# Revit family: Basin-Pedestal-American_Standard-Estate-0900_Series
name_source: partatom
category: Plumbing Fixtures
revit_build: Autodesk Revit 2014 (Build: 20130308_1515(x64)
units: mm (PartAtom-declared; Revit-internal decimal feet)

## types (24) — shared parameters
ADA Compliant = Yes
Assembly Code = D2010310
Basin Shape = Rectangle
CW Connection = Yes
CWFU = 1.5
Cold Water Connection Diameter = 3/8"
Cold Water Connection Height = 24"
Cold Water Connection Radius = 3/16"
Cold Water Connection Width = 4"
Default Elevation = 36 5/8"
Description = Estate Pedestal Bathroom Sink
HW Connection = Yes
HWFU = 1.5
Height = 7 1/2"
Hot Water Connection Diameter = 3/8"
Hot Water Connection Height = 24"
Hot Water Connection Radius = 3/16"
Hot Water Connection Width = 4"
Length = 20"
Manufacturer = American Standard
Price = Prices may vary. Please consult Manufacturer Representative for most up-to-date price list.
Product Documentation Link = https://www.americanstandard-us.com
Product Page URL = https://www.americanstandard-us.com
URL = http://www.americanstandard-us.com
Vent Connection = No
WFU = 2
Waste Connection = Yes
Waste Connection Diameter = 1 1/4"
Waste Connection Height = 22"
Waste Connection Radius = 5/8"
Width = 24"

## per-type parameters (varying)
| type | 0029.000 Pedestal | Centerset Height | Finish | Hole Punch Location | Installation Type | Material |
| 0900.004.020 | No | 3" | Fire Clay-American Standard-020-White | 4" | Countertop | Fire Clay-American Standard-020-White |
| 0900.008.020 | No | 3" | Fire Clay-American Standard-020-White | 8" | Countertop | Fire Clay-American Standard-020-White |
| 0900.001.020 | No | 9" | Fire Clay-American Standard-020-White | 4" | Countertop | Fire Clay-American Standard-020-White |
| 0900.001.021 | No | 9" | Fire Clay-American Standard-021-Bone | 4" | Countertop | Fire Clay-American Standard-021-Bone |
| 0900.001.178 | No | 9" | Fire Clay-American Standard-178-Black | 4" | Countertop | Fire Clay-American Standard-178-Black |
| 0900.001.222 | No | 9" | Fire Clay-American Standard-222-Linen | 4" | Countertop | Fire Clay-American Standard-222-Linen |
| 0900.004.021 | No | 3" | Fire Clay-American Standard-021-Bone | 4" | Countertop | Fire Clay-American Standard-021-Bone |
| 0900.004.178 | No | 3" | Fire Clay-American Standard-178-Black | 4" | Countertop | Fire Clay-American Standard-178-Black |
| 0900.004.222 | No | 3" | Fire Clay-American Standard-222-Linen | 4" | Countertop | Fire Clay-American Standard-222-Linen |
| 0900.008.021 | No | 3" | Fire Clay-American Standard-021-Bone | 8" | Countertop | Fire Clay-American Standard-021-Bone |
| 0900.008.178 | No | 3" | Fire Clay-American Standard-178-Black | 8" | Countertop | Fire Clay-American Standard-178-Black |
| 0900.008.222 | No | 3" | Fire Clay-American Standard-222-Linen | 8" | Countertop | Fire Clay-American Standard-222-Linen |
| 0900.100.020 | Yes | 9" | Fire Clay-American Standard-020-White | 4" | Pedestal | Fire Clay-American Standard-020-White |
| 0900.100.021 | Yes | 9" | Fire Clay-American Standard-021-Bone | 4" | Pedestal | Fire Clay-American Standard-021-Bone |
| 0900.100.178 | Yes | 9" | Fire Clay-American Standard-178-Black | 4" | Pedestal | Fire Clay-American Standard-178-Black |
| 0900.100.222 | Yes | 9" | Fire Clay-American Standard-222-Linen | 4" | Pedestal | Fire Clay-American Standard-222-Linen |
| 0900.400.020 | Yes | 3" | Fire Clay-American Standard-020-White | 4" | Pedestal | Fire Clay-American Standard-020-White |
| 0900.400.021 | Yes | 3" | Fire Clay-American Standard-021-Bone | 4" | Pedestal | Fire Clay-American Standard-021-Bone |
| 0900.400.178 | Yes | 3" | Fire Clay-American Standard-178-Black | 4" | Pedestal | Fire Clay-American Standard-178-Black |
| 0900.400.222 | Yes | 3" | Fire Clay-American Standard-222-Linen | 4" | Pedestal | Fire Clay-American Standard-222-Linen |
| 0900.800.020 | Yes | 3" | Fire Clay-American Standard-020-White | 8" | Pedestal | Fire Clay-American Standard-020-White |
| 0900.800.021 | Yes | 3" | Fire Clay-American Standard-021-Bone | 8" | Pedestal | Fire Clay-American Standard-021-Bone |
| 0900.800.178 | Yes | 3" | Fire Clay-American Standard-178-Black | 8" | Pedestal | Fire Clay-American Standard-178-Black |
| 0900.800.222 | Yes | 3" | Fire Clay-American Standard-222-Linen | 8" | Pedestal | Fire Clay-American Standard-222-Linen |

note: column(s) folded — value = type name in every type: Model

## geometry (parser evidence)
native form markers: Sweep x3
no freeform markers — native parametric forms only
